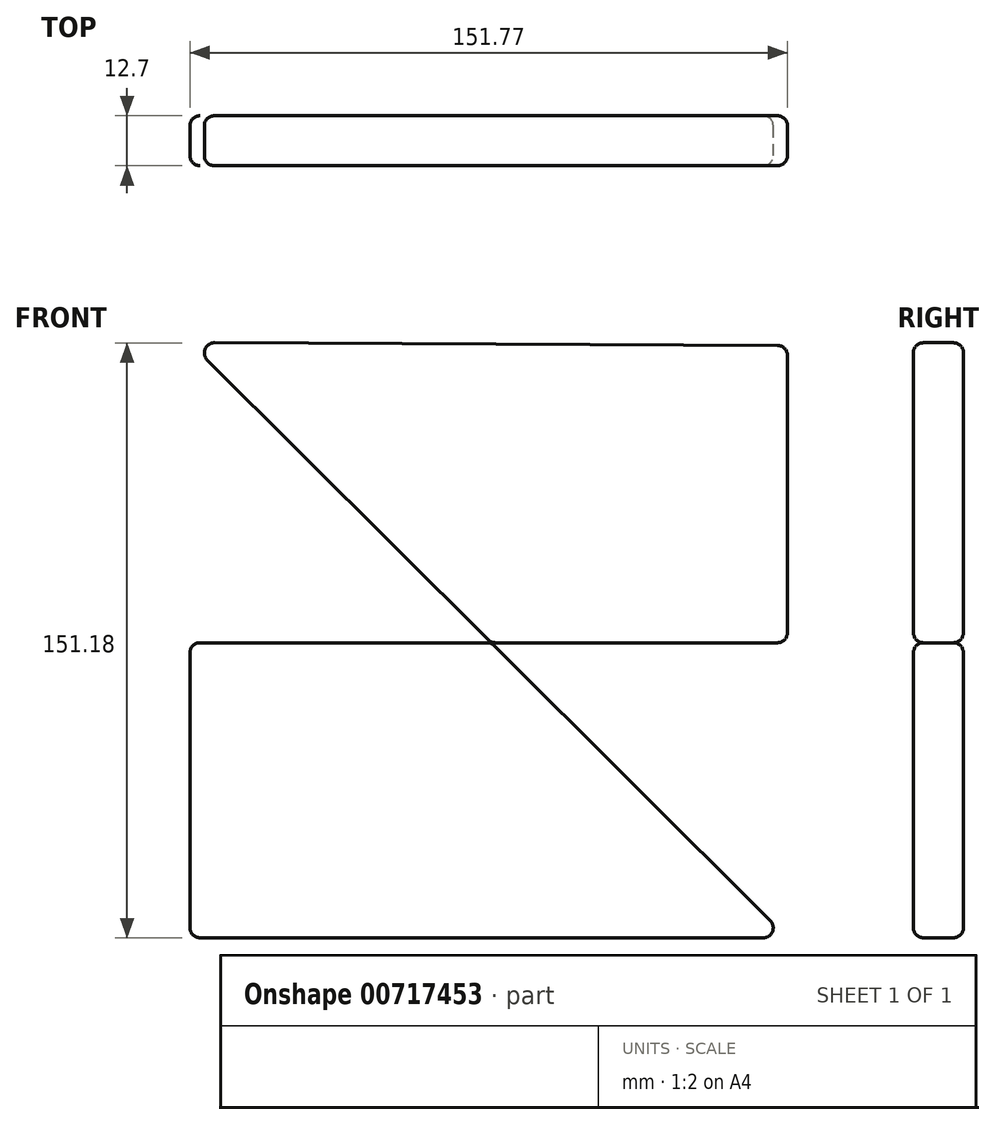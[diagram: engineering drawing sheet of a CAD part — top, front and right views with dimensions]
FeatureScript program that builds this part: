
annotation { "Feature Type Name" : "Feature", "Feature Type Description" : "" }
export const myFeature = defineFeature(function(context is Context, id is Id, definition is map)
    precondition{}
    {
        {
            var Q0;
            Q0=qCreatedBy(makeId("Front.planeOp"),FACE);
            var sketch = newSketch(context, id + "F0", { "sketchPlane" : qUnion([Q0])});
            skLineSegment(sketch, "E0", {"start": v(-76.51, 76.23) * mm, "end": v(0, 0) * mm});
            skLineSegment(sketch, "E1", {"start": v(0, 0) * mm, "end": v(75.26, 75.53) * mm});
            skLineSegment(sketch, "E2", {"start": v(75.26, 75.53) * mm, "end": v(-76.51, 76.23) * mm});
            skLineSegment(sketch, "E3", {"start": v(0, 0) * mm, "end": v(75.26, -74.98) * mm});
            skLineSegment(sketch, "E4", {"start": v(75.26, -74.98) * mm, "end": v(-76.51, -74.98) * mm});
            skLineSegment(sketch, "E5", {"start": v(-76.51, -74.98) * mm, "end": v(0, 0) * mm});
            skLineSegment(sketch, "E6", {"start": v(75.26, 75.53) * mm, "end": v(75.26, 0) * mm});
            skLineSegment(sketch, "E7", {"start": v(75.26, 0) * mm, "end": v(0, 0) * mm});
            skLineSegment(sketch, "E8", {"start": v(0, 0) * mm, "end": v(-76.51, 0) * mm});
            skLineSegment(sketch, "E9", {"start": v(-76.51, 0) * mm, "end": v(-76.51, -74.98) * mm});
            skSolve(sketch);
        }
        {
            var Q0;
            Q0=makeQuery(id+"F0.imprint","IMPRINT",FACE,{"disambiguationData":[TD([[makeQuery(id+"F0.imprint","IMPRINT",EDGE,{"derivedFrom":sQuery(id+"F0.wireOp",EDGE,"E3")}),-1.0]])]});
            var Q1;
            Q1=makeQuery(id+"F0.imprint","IMPRINT",FACE,{"disambiguationData":[TD([[makeQuery(id+"F0.imprint","IMPRINT",EDGE,{"derivedFrom":sQuery(id+"F0.wireOp",EDGE,"E5")}),1.0]])]});
            var Q2;
            Q2=makeQuery(id+"F0.imprint","IMPRINT",FACE,{"disambiguationData":[TD([[makeQuery(id+"F0.imprint","IMPRINT",EDGE,{"derivedFrom":sQuery(id+"F0.wireOp",EDGE,"E1")}),-1.0]])]});
            var Q3;
            Q3=makeQuery(id+"F0.imprint","IMPRINT",FACE,{"disambiguationData":[TD([[makeQuery(id+"F0.imprint","IMPRINT",EDGE,{"derivedFrom":sQuery(id+"F0.wireOp",EDGE,"E0")}),1.0]])]});
            extrude(context, id + "F1", {"entities" : qUnion([Q0, Q1, Q2, Q3]), "depth" : 12.7 * mm, "offsetDistance" : 25.4 * mm});
        }
        {
            var Q0;
            Q0=makeQuery(id+"F1.opExtrude","SWEPT_FACE",FACE,{"disambiguationData":[OSD([sQuery(id+"F0.wireOp",EDGE,"E0")])]});
            var Q1;
            Q1=makeQuery(id+"F1.opExtrude","SWEPT_FACE",FACE,{"disambiguationData":[OSD([sQuery(id+"F0.wireOp",EDGE,"E2")])]});
            var Q2;
            Q2=makeQuery(id+"F1.opExtrude","SWEPT_FACE",FACE,{"disambiguationData":[OSD([sQuery(id+"F0.wireOp",EDGE,"E6")])]});
            var Q3;
            Q3=makeQuery(id+"F1.opExtrude","SWEPT_FACE",FACE,{"disambiguationData":[OSD([sQuery(id+"F0.wireOp",EDGE,"E7")])]});
            fillet(context, id + "F2", {"entities" : qUnion([Q0, Q1, Q2, Q3]), "radius" : 2.54 * mm, "tangentPropagation" : true, "allowEdgeOverflow" : false});
        }
        {
            var Q0;
            Q0=makeQuery(id+"F1.opExtrude","SWEPT_FACE",FACE,{"disambiguationData":[OSD([sQuery(id+"F0.wireOp",EDGE,"E9")])]});
            var Q1;
            Q1=makeQuery(id+"F1.opExtrude","SWEPT_FACE",FACE,{"disambiguationData":[OSD([sQuery(id+"F0.wireOp",EDGE,"E8")])]});
            var Q2;
            Q2=makeQuery(id+"F1.opExtrude","SWEPT_FACE",FACE,{"disambiguationData":[OSD([sQuery(id+"F0.wireOp",EDGE,"E4")])]});
            var Q3;
            Q3=makeQuery(id+"F1.opExtrude","SWEPT_FACE",FACE,{"disambiguationData":[OSD([sQuery(id+"F0.wireOp",EDGE,"E3")])]});
            fillet(context, id + "F3", {"entities" : qUnion([Q0, Q1, Q2, Q3]), "radius" : 2.54 * mm, "tangentPropagation" : true, "allowEdgeOverflow" : false});
        }
    });
